# Revit family: Post Mounted
name_source: partatom
category: Generic Models
revit_build: Autodesk Revit 2017 (Build: 20190508_0315(x64)
units: mm (PartAtom-declared; Revit-internal decimal feet)

## family parameters
Always vertical = Yes
Can host rebar = No
Cut with Voids When Loaded = No
OmniClass Number = 23.25.40.21.17.24
OmniClass Title = Panel Fences
Part Type = Normal
Room Calculation Point = No
Round Connector Dimension = Use Diameter
Shared = No
Work Plane-Based = No

## types (2) — shared parameters
Arch Height = 1' - 0"
Assembly Description = Fences & Gates
Description = Post Mounted Nature Screen
Double Layer = Yes
End Post Finish = <By Category>
Foliage Material = Nature Screen Foliage
Frame Depth = 0' - 3"
Frame Finish = <By Category>
LED Light = Nature Screen Light Source
LED Lights = Yes
Layer One Location = 0' - 0 1/8"
Manufacturer = CityScapes
Max Area = 51.78 SF
Max Height = 10' - 1 1/4"
Max Width = 10' - 1 1/4"
Model = Nature Screen
Post Extension = 0' - 2"
Screen Material = Nature Screen 2"x2"
Screen Offset From Ground = 1' - 0"
Single Layer = No
URL = https://cityscapesinc.com
Version = 191001

## per-type parameters (varying)
| type | 4x4 Post | 6x6 Post | Arched Top | Arched Top Double | Assembly Code | Direct Buried Post | Flat Top | Flat Top Double | LED Arched Top | LED Flat Top | Post Buried Depth | Post Size | Surface Mounted Post |
| Flat Top | No | Yes | No | No | G2040100 | No | Yes | Yes | No | Yes | 0' - 0" | 0' - 5 1/2" | Yes |
| Arch Top | Yes | No | Yes | Yes |  | Yes | No | No | Yes | No | 2' - 6" | 0' - 3 1/2" | No |

## geometry (parser evidence)
native form markers: Sweep x2
no freeform markers — native parametric forms only
